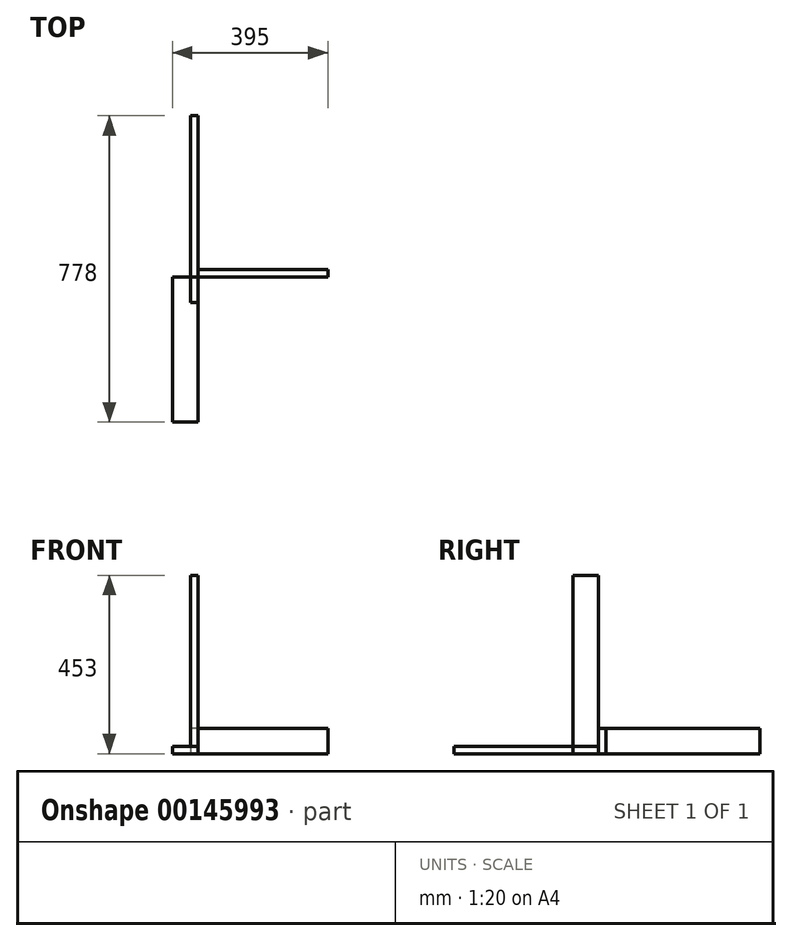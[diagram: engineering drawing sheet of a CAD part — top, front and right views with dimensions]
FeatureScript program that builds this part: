
annotation { "Feature Type Name" : "Feature", "Feature Type Description" : "" }
export const myFeature = defineFeature(function(context is Context, id is Id, definition is map)
    precondition{}
    {
        {
            var Q0;
            Q0=qCreatedBy(makeId("Right.planeOp"),FACE);
            var sketch = newSketch(context, id + "F0", { "sketchPlane" : qUnion([Q0])});
            skLineSegment(sketch, "E0", {"start": v(0, 0) * mm, "end": v(0, 65) * mm});
            skLineSegment(sketch, "E1", {"start": v(0, 65) * mm, "end": v(19, 65) * mm});
            skLineSegment(sketch, "E2", {"start": v(19, 65) * mm, "end": v(19, 0) * mm});
            skLineSegment(sketch, "E3", {"start": v(19, 0) * mm, "end": v(0, 0) * mm});
            skSolve(sketch);
        }
        {
            var Q0;
            Q0=makeQuery(id+"F0.imprint","IMPRINT",FACE,{"disambiguationData":[TD([[makeQuery(id+"F0.imprint","IMPRINT",EDGE,{"derivedFrom":sQuery(id+"F0.wireOp",EDGE,"E0")}),-1.0]])]});
            var Q1;
            Q1 = qSketchRegion(id + "F2", true);
            extrude(context, id + "F1", {"entities" : qUnion([Q0, Q1]), "depth" : (350 - 20) * mm});
        }
        {
            var Q0;
            Q0=qCreatedBy(makeId("Top.planeOp"),FACE);
            var sketch = newSketch(context, id + "F2", { "sketchPlane" : qUnion([Q0])});
            skLineSegment(sketch, "E4.bottom", {"start": v(0, 0) * mm, "end": v(-19, 0) * mm});
            skLineSegment(sketch, "E4.top", {"start": v(0, -65) * mm, "end": v(-19, -65) * mm});
            skLineSegment(sketch, "E4.left", {"start": v(0, 0) * mm, "end": v(0, -65) * mm});
            skLineSegment(sketch, "E4.right", {"start": v(-19, 0) * mm, "end": v(-19, -65) * mm});
            skSolve(sketch);
        }
        {
            var Q0;
            Q0=qCreatedBy(makeId("Front.planeOp"),FACE);
            var sketch = newSketch(context, id + "F3", { "sketchPlane" : qUnion([Q0])});
            skLineSegment(sketch, "E5.bottom", {"start": v(0, 0) * mm, "end": v(-19, 0) * mm});
            skLineSegment(sketch, "E5.top", {"start": v(0, 65) * mm, "end": v(-19, 65) * mm});
            skLineSegment(sketch, "E5.left", {"start": v(0, 0) * mm, "end": v(0, 65) * mm});
            skLineSegment(sketch, "E5.right", {"start": v(-19, 0) * mm, "end": v(-19, 65) * mm});
            skSolve(sketch);
        }
        {
            var Q0;
            Q0 = qSketchRegion(id + "F3", true);
            extrude(context, id + "F4", {"entities" : qUnion([Q0]), "oppositeDirection" : true, "depth" : 410 * mm});
        }
        {
            var Q0;
            Q0 = qSketchRegion(id + "F2", true);
            extrude(context, id + "F5", {"entities" : qUnion([Q0]), "depth" : (47 + 406) * mm});
        }
        {
            var Q0;
            Q0=qCreatedBy(makeId("Front.planeOp"),FACE);
            var sketch = newSketch(context, id + "F6", { "sketchPlane" : qUnion([Q0])});
            skLineSegment(sketch, "E6.bottom", {"start": v(0, 0) * mm, "end": v(-65, 0) * mm});
            skLineSegment(sketch, "E6.top", {"start": v(0, 19) * mm, "end": v(-65, 19) * mm});
            skLineSegment(sketch, "E6.left", {"start": v(0, 0) * mm, "end": v(0, 19) * mm});
            skLineSegment(sketch, "E6.right", {"start": v(-65, 0) * mm, "end": v(-65, 19) * mm});
            skSolve(sketch);
        }
        {
            var Q0;
            Q0 = qSketchRegion(id + "F6", true);
            extrude(context, id + "F7", {"entities" : qUnion([Q0]), "depth" : (350 - 20 + 38) * mm});
        }
    });
